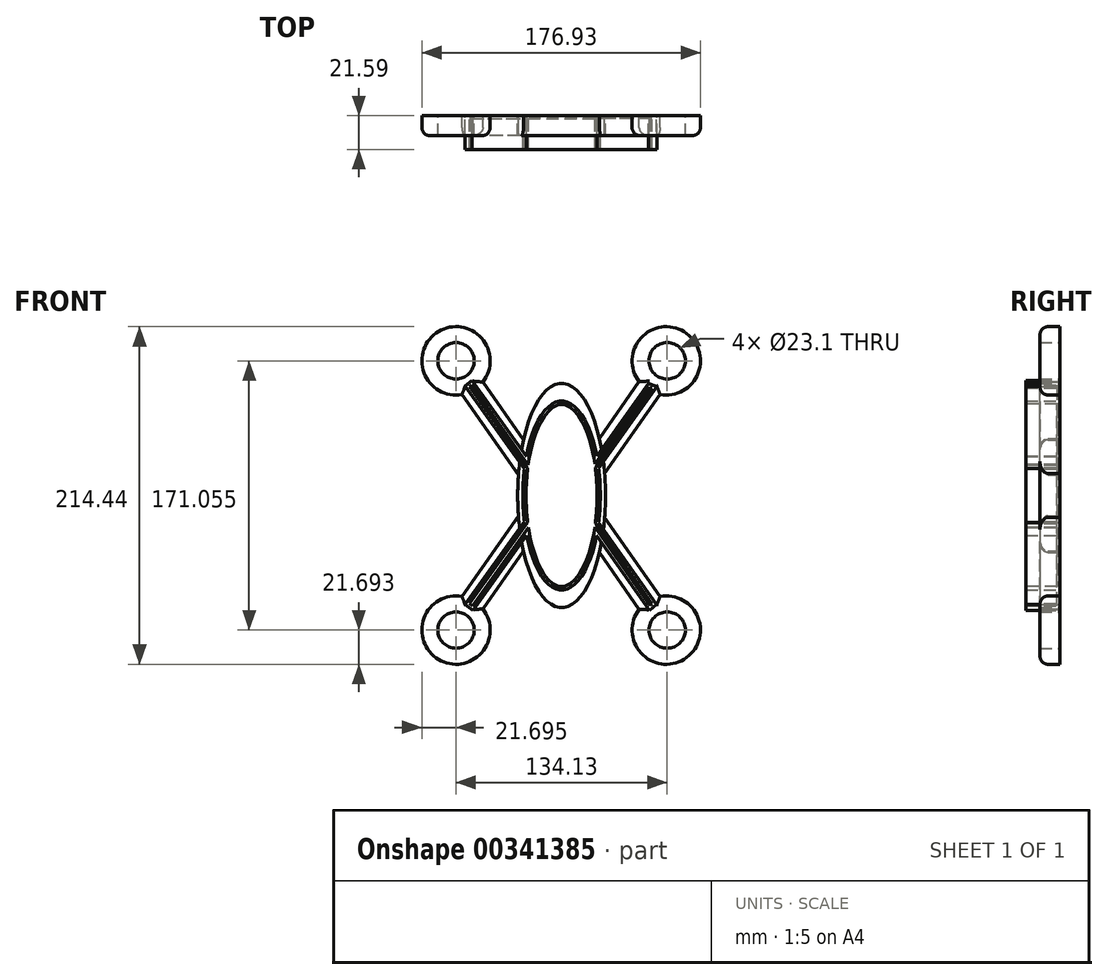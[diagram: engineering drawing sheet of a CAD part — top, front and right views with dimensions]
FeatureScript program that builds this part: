
annotation { "Feature Type Name" : "Feature", "Feature Type Description" : "" }
export const myFeature = defineFeature(function(context is Context, id is Id, definition is map)
    precondition{}
    {
        {
            var Q0;
            Q0=qCreatedBy(makeId("Front.planeOp"),FACE);
            var sketch = newSketch(context, id + "F0", { "sketchPlane" : qUnion([Q0])});
            skEllipse(sketch, "E0", {"center": v(0, 0) * mm, "majorRadius": 71.2 * mm, "minorRadius": 27.89 * mm, "majorAxis": v(0, -1)});
            skLineSegment(sketch, "E1.bottom", {"start": v(-14.74, 21.83) * mm, "end": v(-27.42, 12.95) * mm});
            skLineSegment(sketch, "E1.left", {"start": v(-14.74, 21.83) * mm, "end": v(-54.39, 78.44) * mm});
            skLineSegment(sketch, "E1.right", {"start": v(-27.42, 12.95) * mm, "end": v(-67.06, 69.56) * mm});
            skLineSegment(sketch, "E2.bottom", {"start": v(26.83, 13.26) * mm, "end": v(14.15, 22.14) * mm});
            skLineSegment(sketch, "E2.left", {"start": v(26.83, 13.26) * mm, "end": v(66.48, 69.87) * mm});
            skLineSegment(sketch, "E2.right", {"start": v(14.15, 22.14) * mm, "end": v(53.8, 78.75) * mm});
            skLineSegment(sketch, "E3", {"start": v(-14.74, 21.83) * mm, "end": v(0, 21.83) * mm});
            skLineSegment(sketch, "E4", {"start": v(0, 21.83) * mm, "end": v(14.15, 22.14) * mm});
            skLineSegment(sketch, "E5.MirrorCS", {"start": v(-14.74, -21.83) * mm, "end": v(-27.42, -12.95) * mm});
            skLineSegment(sketch, "E6.MirrorCS", {"start": v(-14.74, -21.83) * mm, "end": v(-54.39, -78.44) * mm});
            skLineSegment(sketch, "E7.MirrorCS", {"start": v(-27.42, -12.95) * mm, "end": v(-67.06, -69.56) * mm});
            skLineSegment(sketch, "E8.MirrorCS", {"start": v(-14.74, -21.83) * mm, "end": v(0, -21.83) * mm});
            skLineSegment(sketch, "E9.MirrorCS", {"start": v(0, -21.83) * mm, "end": v(14.15, -22.14) * mm});
            skLineSegment(sketch, "E10.MirrorCS", {"start": v(14.15, -22.14) * mm, "end": v(53.8, -78.75) * mm});
            skLineSegment(sketch, "E11.MirrorCS", {"start": v(26.83, -13.26) * mm, "end": v(66.48, -69.87) * mm});
            skLineSegment(sketch, "E12.MirrorCS", {"start": v(26.83, -13.26) * mm, "end": v(14.15, -22.14) * mm});
            skCircle(sketch, "E13", {"center": v(-67.06, 85.53) * mm, "radius": 21.7 * mm});
            skCircle(sketch, "E14", {"center": v(66.48, 85.53) * mm, "radius": 21.7 * mm});
            skCircle(sketch, "E15.MirrorC", {"center": v(-67.06, -85.53) * mm, "radius": 21.7 * mm});
            skCircle(sketch, "E16.MirrorC", {"center": v(66.48, -85.53) * mm, "radius": 21.7 * mm});
            skCircle(sketch, "E17", {"center": v(-67.06, 85.53) * mm, "radius": 11.55 * mm});
            skCircle(sketch, "E18.MirrorC", {"center": v(67.06, 85.53) * mm, "radius": 11.55 * mm});
            skCircle(sketch, "E19.MirrorC", {"center": v(-67.06, -85.53) * mm, "radius": 11.55 * mm});
            skCircle(sketch, "E20.MirrorC", {"center": v(67.06, -85.53) * mm, "radius": 11.55 * mm});
            skSolve(sketch);
        }
        {
            var Q0;
            Q0=qSketchRegion(id+"F0",true);
            extrude(context, id + "F1", {"entities" : qUnion([Q0]), "depth" : 12.7 * mm});
        }
        {
            var Q0;
            Q0=makeQuery(id+"F1.opExtrude","CAP_EDGE",EDGE,{"disambiguationData":[OSD([sQuery(id+"F0.wireOp",EDGE,"E13")])],"isStart":false});
            var Q1;
            Q1=makeQuery(id+"F1.opExtrude","CAP_EDGE",EDGE,{"disambiguationData":[OSD([sQuery(id+"F0.wireOp",EDGE,"E14")])],"isStart":false});
            var Q2;
            Q2=makeQuery(id+"F1.opExtrude","CAP_EDGE",EDGE,{"disambiguationData":[OSD([sQuery(id+"F0.wireOp",EDGE,"E16.MirrorC")])],"isStart":false});
            var Q3;
            Q3=makeQuery(id+"F1.opExtrude","CAP_EDGE",EDGE,{"disambiguationData":[OSD([sQuery(id+"F0.wireOp",EDGE,"E15.MirrorC")])],"isStart":false});
            fillet(context, id + "F2", {"entities" : qUnion([Q0, Q1, Q2, Q3]), "radius" : 5.08 * mm, "tangentPropagation" : true, "allowEdgeOverflow" : false});
        }
        {
            var Q0;
            Q0=makeQuery(id+"F1.opExtrude","CAP_EDGE",EDGE,{"disambiguationData":[OSD([sQuery(id+"F0.wireOp",EDGE,"E1.right")])],"isStart":false});
            var Q1;
            Q1=makeQuery(id+"F1.opExtrude","CAP_EDGE",EDGE,{"disambiguationData":[OSD([sQuery(id+"F0.wireOp",EDGE,"E1.left")])],"isStart":false});
            var Q2;
            Q2=makeQuery(id+"F1.opExtrude","CAP_EDGE",EDGE,{"disambiguationData":[OSD([sQuery(id+"F0.wireOp",EDGE,"E2.right")])],"isStart":false});
            var Q3;
            Q3=makeQuery(id+"F1.opExtrude","CAP_EDGE",EDGE,{"disambiguationData":[OSD([sQuery(id+"F0.wireOp",EDGE,"E2.left")])],"isStart":false});
            var Q4;
            Q4=makeQuery(id+"F1.opExtrude","CAP_EDGE",EDGE,{"disambiguationData":[OSD([sQuery(id+"F0.wireOp",EDGE,"E11.MirrorCS")])],"isStart":false});
            var Q5;
            Q5=makeQuery(id+"F1.opExtrude","CAP_EDGE",EDGE,{"disambiguationData":[OSD([sQuery(id+"F0.wireOp",EDGE,"E10.MirrorCS")])],"isStart":false});
            var Q6;
            Q6=makeQuery(id+"F1.opExtrude","CAP_EDGE",EDGE,{"disambiguationData":[OSD([sQuery(id+"F0.wireOp",EDGE,"E6.MirrorCS")])],"isStart":false});
            var Q7;
            Q7=makeQuery(id+"F1.opExtrude","CAP_EDGE",EDGE,{"disambiguationData":[OSD([sQuery(id+"F0.wireOp",EDGE,"E7.MirrorCS")])],"isStart":false});
            fillet(context, id + "F3", {"entities" : qUnion([Q0, Q1, Q2, Q3, Q4, Q5, Q6, Q7]), "radius" : 5.08 * mm, "tangentPropagation" : true, "allowEdgeOverflow" : false});
        }
        {
            var Q0;
            Q0=qCreatedBy(makeId("Front.planeOp"),FACE);
            var sketch = newSketch(context, id + "F4", { "sketchPlane" : qUnion([Q0])});
            skEllipse(sketch, "E21", {"center": v(0, 0) * mm, "majorRadius": 59.97 * mm, "minorRadius": 24.6 * mm, "majorAxis": v(0, -1)});
            skLineSegment(sketch, "E22", {"start": v(-61.2, -69.14) * mm, "end": v(-23.64, -16.51) * mm});
            skLineSegment(sketch, "E23", {"start": v(-56.28, -72.98) * mm, "end": v(-22.28, -25.36) * mm});
            skLineSegment(sketch, "E24", {"start": v(-22.28, -25.36) * mm, "end": v(-23.64, -16.51) * mm});
            skLineSegment(sketch, "E25", {"start": v(-56.28, -72.98) * mm, "end": v(-61.2, -69.14) * mm});
            skLineSegment(sketch, "E26", {"start": v(55.93, -72.98) * mm, "end": v(22.28, -25.36) * mm});
            skLineSegment(sketch, "E27", {"start": v(60.27, -69.12) * mm, "end": v(23.56, -17.18) * mm});
            skLineSegment(sketch, "E28", {"start": v(-61.21, 69.6) * mm, "end": v(-23.6, 16.78) * mm});
            skLineSegment(sketch, "E29", {"start": v(-56.76, 72.95) * mm, "end": v(-22.4, 24.7) * mm});
            skLineSegment(sketch, "E30", {"start": v(-61.21, 69.6) * mm, "end": v(-56.76, 72.95) * mm});
            skLineSegment(sketch, "E31", {"start": v(55.11, 71.04) * mm, "end": v(60.5, 69.13) * mm});
            skLineSegment(sketch, "E32", {"start": v(55.93, -72.98) * mm, "end": v(60.27, -69.12) * mm});
            skLineSegment(sketch, "E33", {"start": v(60.5, 69.13) * mm, "end": v(23.55, 17.24) * mm});
            skLineSegment(sketch, "E34", {"start": v(55.11, 71.04) * mm, "end": v(22.34, 25.06) * mm});
            skSolve(sketch);
        }
        {
            var Q0;
            Q0=qSketchRegion(id+"F4",true);
            extrude(context, id + "F5", {"entities" : qUnion([Q0]), "depth" : 21.59 * mm});
        }
        {
            var Q0;
            Q0=makeQuery(id+"F5.opExtrude","CAP_FACE",FACE,{"disambiguationData":[OSD([sQuery(id+"F4.wireOp",EDGE,"E21"),sQuery(id+"F4.wireOp",EDGE,"NEgBn6b3-1pjr-pe8X-6l68-krjNJmOewhNc"),sQuery(id+"F4.wireOp",EDGE,"9DAIEF9t-jXmu-CJTj-gN3L-F5fUEMQPX4Ks"),sQuery(id+"F4.wireOp",EDGE,"E22"),sQuery(id+"F4.wireOp",EDGE,"E23"),sQuery(id+"F4.wireOp",EDGE,"E25"),sQuery(id+"F4.wireOp",EDGE,"E26"),sQuery(id+"F4.wireOp",EDGE,"E27"),sQuery(id+"F4.wireOp",EDGE,"E28"),sQuery(id+"F4.wireOp",EDGE,"E29"),sQuery(id+"F4.wireOp",EDGE,"E30"),sQuery(id+"F4.wireOp",EDGE,"E31"),sQuery(id+"F4.wireOp",EDGE,"E32")])],"isStart":false});
            shell(context, id + "F6", {"entities" : qUnion([Q0]), "thickness" : 2.03 * mm});
        }
    });
